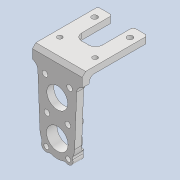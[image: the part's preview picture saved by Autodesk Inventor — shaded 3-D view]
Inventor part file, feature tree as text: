
AUTODESK INVENTOR PART (.ipt)
format: ipt  version: 2020 (Build 240168000, 168)  size: 429,568 bytes
history: native  units: mm
features: projected_geometry x14, sketch x11, extrude x10, reference x10, fillet x7, other x6, chamfer x2, hole x1, thicken_offset x1
ambient origin geometry x8: Origin, YZ Plane, XZ Plane, XY Plane, X Axis, Y Axis, Z Axis, Center Point
bodies: Solid1 (feature_tree)
feature tree (62):
  extrude  "Extrusion1"  Depth=6.0mm
  extrude  "Extrusion2"  Depth=10.0mm
  extrude  "Extrusion3"  Depth=1.5mm
  extrude  "Extrusion4"  Depth=4.15mm
  extrude  "Extrusion5"  Depth=4.15mm
  extrude  "Extrusion6"  Depth=6.0mm TaperAngle=0.0deg
  fillet  "Fillet1"  Radius=17.5mm
  fillet  "Fillet2"  Radius=6.0mm
  chamfer  "Chamfer1"  Distance=6.0mm
  fillet  "Fillet3"  Radius=8.5mm
  fillet  "Fillet4"  Radius=1.0mm
  fillet  "Fillet5"  Radius=1.0mm
  extrude  "Extrusion8"  Depth=3.0mm
  hole  "Hole1"  [1 undecoded]
  fillet  "Fillet6"  Radius=1.5mm
  extrude  "Extrusion9"  Depth=3.0mm
  thicken_offset  "Thicken1"
  chamfer  "Chamfer2"  Distance=2.0mm
  extrude  "Extrusion10"  Depth=6.0mm
  fillet  "Fillet7"  Radius=6.0mm
  extrude  "Extrusion11"  TaperAngle=30.0deg  [1 undecoded]
  sketch  "Sketch1"  dims[d0=6.0mm d1=6.0mm]
  reference  "Reference1"
  reference  "Reference2"
  reference  "Reference3"
  reference  "Reference4"
  reference  "Reference5"
  sketch  "Sketch2"  dims[d2=8.5mm d3=10.0mm]
  projected_geometry  "Projected Loop1"
  reference  "Reference6"
  sketch  "Sketch3"  dims[d4=1.5mm d5=1.5mm]
  reference  "Reference7"
  projected_geometry  "Projected Loop2"
  projected_geometry  "Projected Loop3"
  projected_geometry  "Projected Loop4"
  sketch  "Sketch4"  dims[d6=2.0mm d7=0.0mm d8=4.15mm]
  projected_geometry  "Projected Loop5"
  sketch  "Sketch5"  dims[d9=18.8mm d10=4.15mm]
  projected_geometry  "Projected Loop6"
  reference  "Reference8"
  reference  "Reference9"
  sketch  "Sketch6"  dims[d11=18.8mm d12=1.8mm d13=0.0mm d14=17.5mm d15=6.0mm d16=0.0mm]
  reference  "Reference10"
  sketch  "Sketch8"  dims[d17=3.0mm]
  projected_geometry  "Projected Loop7"
  sketch  "Sketch9"  dims[d18=1.6mm]
  projected_geometry  "Projected Loop8"
  projected_geometry  "Projected Loop9"
  projected_geometry  "Projected Loop10"
  sketch  "Sketch10"  dims[d19=3.0mm]
  projected_geometry  "Projected Loop11"
  projected_geometry  "Projected Loop12"
  sketch  "Sketch11"  dims[d20=1.6mm d21=6.0mm d22=0.0mm d23=8.5mm d24=1.0mm d25=0.0mm d26=1.0mm d27=0.0mm]
  projected_geometry  "Projected Loop13"
  sketch  "Sketch12"  dims[d30=1.0mm d31=1.5mm d32=1.0mm d33=2.0mm d34=45.0deg d35=1.5mm d36=2.0mm d37=2.0mm d38=6.0mm d39=6.0mm d40=30.0deg d41=30.0deg d42=5.5mm d43=5.5mm d44=6.981317mm d45=6.981317mm d46=3.0mm d47=3.0mm d48=3.0mm d49=3.0mm d50=3.0mm d51=3.0mm d52=1.0mm d53=0.0mm d54=1.6mm d55=6.0mm d56=4.0mm d57=2.0mm d58=90.0deg d59=5.0mm d60=0.0mm d61=1.0mm d62=10.15mm d63=10.0mm d64=1.4mm d65=1.4mm d66=3.0mm d67=0.0mm d68=0.1mm d69=0.15mm d70=0.5mm d71=2.0mm d72=45.0deg d73=7.330383mm d74=7.330383mm d75=0.3mm d76=2.8mm d77=0.3mm d78=2.8mm d79=3.0mm d80=0.0mm d81=1.0mm d82=1.4mm d83=1.4mm d84=3.0mm d85=0.0mm]
  projected_geometry  "Projected Loop14"
  parser-record x1  (decoder bookkeeping rows leaked as tree rows — omitted from the tree; the rows remain in map.json)
  other  "tip_ass_t1.iam"
  other  "motor_1608:1"
  other  "motor_1608_outer:1"
  other  "bearing_3_6_2:3"
  other  "pin_conn_1:1"
note: 2 required parameter values undecoded (feature->parameter linkage not recoverable at this tier; creation-order binding heuristic only, values carry confidence <= 0.55)
note: 1 file-system path scrubbed to <path> (originals preserved in map.json)
